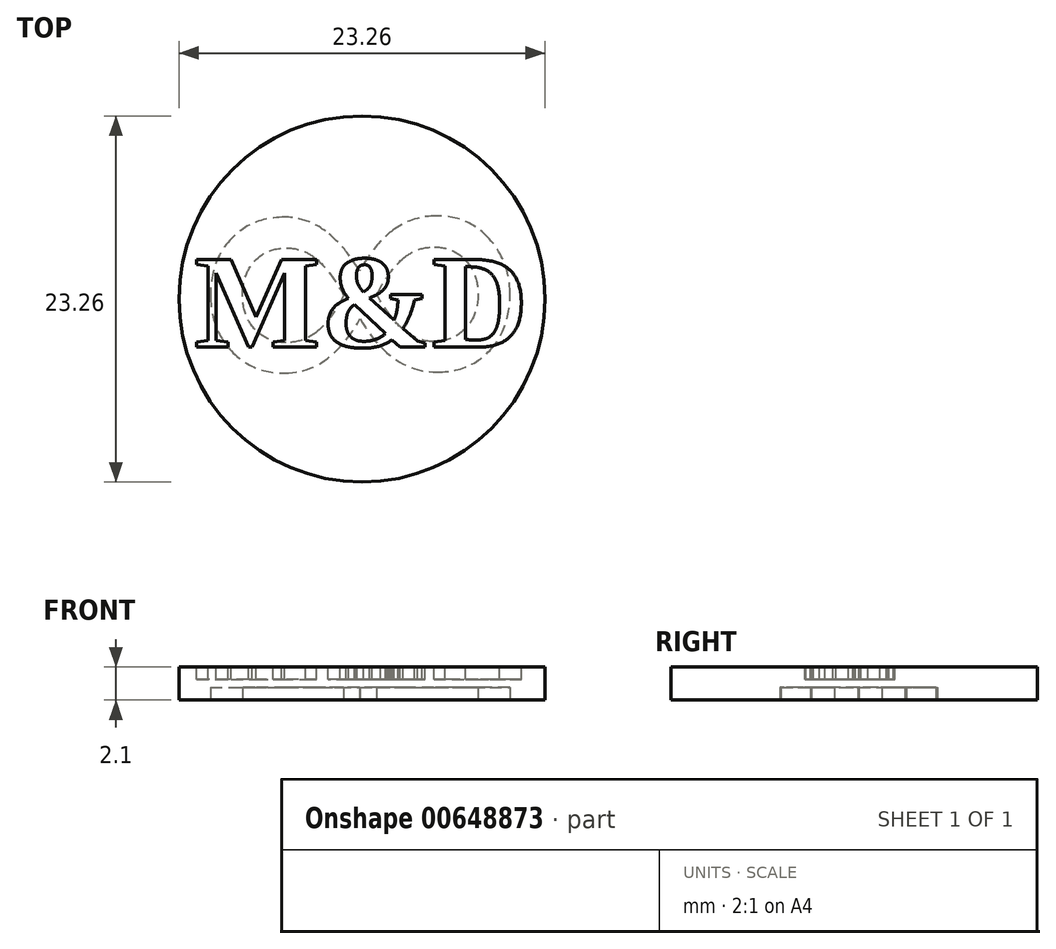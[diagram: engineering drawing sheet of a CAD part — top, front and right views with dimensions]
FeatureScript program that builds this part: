
annotation { "Feature Type Name" : "Feature", "Feature Type Description" : "" }
export const myFeature = defineFeature(function(context is Context, id is Id, definition is map)
    precondition{}
    {
        {
            var Q0;
            Q0=qCreatedBy(makeId("Top.planeOp"),FACE);
            var sketch = newSketch(context, id + "F0", { "sketchPlane" : qUnion([Q0])});
            skCircle(sketch, "E0", {"center": v(0, 0) * mm, "radius": 11.63 * mm});
            skSolve(sketch);
        }
        {
            var Q0;
            Q0=makeQuery(id+"F0.imprint","IMPRINT",FACE,{"disambiguationData":[TD([[makeQuery(id+"F0.imprint","IMPRINT",EDGE,{"derivedFrom":sQuery(id+"F0.wireOp",EDGE,"E0")}),1.0]])]});
            extrude(context, id + "F1", {"entities" : qUnion([Q0]), "depth" : 2.1 * mm, "offsetDistance" : 25 * mm});
        }
        {
            var Q0;
            Q0=makeQuery(id+"F1.opExtrude","CAP_FACE",FACE,{"disambiguationData":[OSD([sQuery(id+"F0.wireOp",EDGE,"E0")])],"isStart":false});
            var sketch = newSketch(context, id + "F2", { "sketchPlane" : qUnion([Q0])});
            skText(sketch, "E1", { "text": "M&D", "fontName": "Tinos-Bold.ttf"});
            skCircle(sketch, "E2.0", {"center": v(0, 0) * mm, "radius": 11.13 * mm});
            skLineSegment(sketch, "E3", {"start": v(10.64, 3.05) * mm, "end": v(-10.64, -3.05) * mm, "construction": true});
            const initialGuessF2  = {"E1": [-0.01064, -0.00305, 1, 0, 0.0061]};
            skSetInitialGuess(sketch, initialGuessF2);
            skSolve(sketch);
        }
        {
            var Q0;
            Q0=makeQuery(id+"F2.imprint","IMPRINT",FACE,{"disambiguationData":[TD([[makeQuery(id+"F2.imprint","IMPRINT",EDGE,{"derivedFrom":sQuery(id+"F2.wireOp",EDGE,"E1.sketch_text.stroke-0")}),-1.0]])]});
            var Q1;
            Q1=makeQuery(id+"F2.imprint","IMPRINT",FACE,{"disambiguationData":[TD([[makeQuery(id+"F2.imprint","IMPRINT",EDGE,{"derivedFrom":sQuery(id+"F2.wireOp",EDGE,"E1.sketch_text.stroke-25")}),-1.0]])]});
            var Q2;
            Q2=makeQuery(id+"F2.imprint","IMPRINT",FACE,{"disambiguationData":[TD([[makeQuery(id+"F2.imprint","IMPRINT",EDGE,{"derivedFrom":sQuery(id+"F2.wireOp",EDGE,"E1.sketch_text.stroke-53")}),-1.0]])]});
            var Q3;
            Q3=makeQuery(id+"F2.imprint","IMPRINT",FACE,{"disambiguationData":[TD([[makeQuery(id+"F2.imprint","IMPRINT",EDGE,{"derivedFrom":sQuery(id+"F2.wireOp",EDGE,"E1.sketch_text.stroke-170")}),-1.0]])]});
            var Q4;
            Q4=makeQuery(id+"F2.imprint","IMPRINT",FACE,{"disambiguationData":[TD([[makeQuery(id+"F2.imprint","IMPRINT",EDGE,{"derivedFrom":sQuery(id+"F2.wireOp",EDGE,"E1.sketch_text.stroke-211")}),-1.0]])]});
            var Q5;
            Q5=makeQuery(id+"F2.imprint","IMPRINT",FACE,{"disambiguationData":[TD([[makeQuery(id+"F2.imprint","IMPRINT",EDGE,{"derivedFrom":sQuery(id+"F2.wireOp",EDGE,"E1.sketch_text.stroke-231")}),-1.0]])]});
            var Q6;
            Q6=makeQuery(id+"F2.imprint","IMPRINT",FACE,{"disambiguationData":[TD([[makeQuery(id+"F2.imprint","IMPRINT",EDGE,{"derivedFrom":sQuery(id+"F2.wireOp",EDGE,"E1.sketch_text.stroke-247")}),-1.0]])]});
            var Q7;
            Q7=makeQuery(id+"F2.imprint","IMPRINT",FACE,{"disambiguationData":[TD([[makeQuery(id+"F2.imprint","IMPRINT",EDGE,{"derivedFrom":sQuery(id+"F2.wireOp",EDGE,"E1.sketch_text.stroke-284")}),-1.0]])]});
            var Q8;
            Q8=makeQuery(id+"F2.imprint","IMPRINT",FACE,{"disambiguationData":[TD([[makeQuery(id+"F2.imprint","IMPRINT",EDGE,{"derivedFrom":sQuery(id+"F2.wireOp",EDGE,"E1.sketch_text.stroke-302")}),-1.0]])]});
            var Q9;
            Q9=makeQuery(id+"F2.imprint","IMPRINT",FACE,{"disambiguationData":[TD([[makeQuery(id+"F2.imprint","IMPRINT",EDGE,{"derivedFrom":sQuery(id+"F2.wireOp",EDGE,"E1.sketch_text.stroke-326")}),-1.0]])]});
            var Q10;
            Q10=makeQuery(id+"F2.imprint","IMPRINT",FACE,{"disambiguationData":[TD([[makeQuery(id+"F2.imprint","IMPRINT",EDGE,{"derivedFrom":sQuery(id+"F2.wireOp",EDGE,"E1.sketch_text.stroke-344")}),-1.0]])]});
            var Q11;
            Q11=makeQuery(id+"F2.imprint","IMPRINT",FACE,{"disambiguationData":[TD([[makeQuery(id+"F2.imprint","IMPRINT",EDGE,{"derivedFrom":sQuery(id+"F2.wireOp",EDGE,"E1.sketch_text.stroke-336")}),-1.0]])]});
            var Q12;
            Q12=makeQuery(id+"F2.imprint","IMPRINT",FACE,{"disambiguationData":[TD([[makeQuery(id+"F2.imprint","IMPRINT",EDGE,{"derivedFrom":sQuery(id+"F2.wireOp",EDGE,"E1.sketch_text.stroke-294")}),-1.0]])]});
            var Q13;
            Q13=makeQuery(id+"F2.imprint","IMPRINT",FACE,{"disambiguationData":[TD([[makeQuery(id+"F2.imprint","IMPRINT",EDGE,{"derivedFrom":sQuery(id+"F2.wireOp",EDGE,"E1.sketch_text.stroke-72")}),-1.0]])]});
            var Q14;
            Q14=makeQuery(id+"F2.imprint","IMPRINT",FACE,{"disambiguationData":[TD([[makeQuery(id+"F2.imprint","IMPRINT",EDGE,{"derivedFrom":sQuery(id+"F2.wireOp",EDGE,"E1.sketch_text.stroke-82")}),-1.0]])]});
            var Q15;
            Q15=makeQuery(id+"F2.imprint","IMPRINT",FACE,{"disambiguationData":[TD([[makeQuery(id+"F2.imprint","IMPRINT",EDGE,{"derivedFrom":sQuery(id+"F2.wireOp",EDGE,"E1.sketch_text.stroke-90")}),-1.0]])]});
            var Q16;
            Q16=makeQuery(id+"F2.imprint","IMPRINT",FACE,{"disambiguationData":[TD([[makeQuery(id+"F2.imprint","IMPRINT",EDGE,{"derivedFrom":sQuery(id+"F2.wireOp",EDGE,"E1.sketch_text.stroke-118")}),-1.0]])]});
            var Q17;
            Q17=makeQuery(id+"F2.imprint","IMPRINT",FACE,{"disambiguationData":[TD([[makeQuery(id+"F2.imprint","IMPRINT",EDGE,{"derivedFrom":sQuery(id+"F2.wireOp",EDGE,"E1.sketch_text.stroke-142")}),-1.0]])]});
            extrude(context, id + "F3", {"entities" : qUnion([Q0, Q1, Q2, Q3, Q4, Q5, Q6, Q7, Q8, Q9, Q10, Q11, Q12, Q13, Q14, Q15, Q16, Q17]), "operationType" : NewBodyOperationType.REMOVE, "oppositeDirection" : true, "depth" : 0.8 * mm, "offsetDistance" : 25 * mm});
        }
        {
            var Q0;
            Q0=makeQuery(id+"F1.opExtrude","CAP_FACE",FACE,{"disambiguationData":[OSD([sQuery(id+"F0.wireOp",EDGE,"E0")])],"isStart":true});
            var sketch = newSketch(context, id + "F4", { "sketchPlane" : qUnion([Q0])});
            skText(sketch, "E4", { "text": "∞", "fontName": "OpenSans-Regular.ttf"});
            skLineSegment(sketch, "E5", {"start": v(11.5, -11.63) * mm, "end": v(-11.5, 11.63) * mm, "construction": true});
            skCircle(sketch, "E6.0", {"center": v(0, 0) * mm, "radius": 11.13 * mm});
            const initialGuessF4  = {"E4": [-0.0115, -0.01163, 1, 0, 0.02326]};
            skSetInitialGuess(sketch, initialGuessF4);
            skSolve(sketch);
        }
        {
            var Q0;
            Q0=makeQuery(id+"F4.imprint","IMPRINT",FACE,{"disambiguationData":[TD([[makeQuery(id+"F4.imprint","IMPRINT",EDGE,{"derivedFrom":sQuery(id+"F4.wireOp",EDGE,"E4.sketch_text.stroke-0")}),-1.0]])]});
            extrude(context, id + "F5", {"entities" : qUnion([Q0]), "operationType" : NewBodyOperationType.REMOVE, "oppositeDirection" : true, "depth" : 0.8 * mm, "offsetDistance" : 25 * mm});
        }
    });
